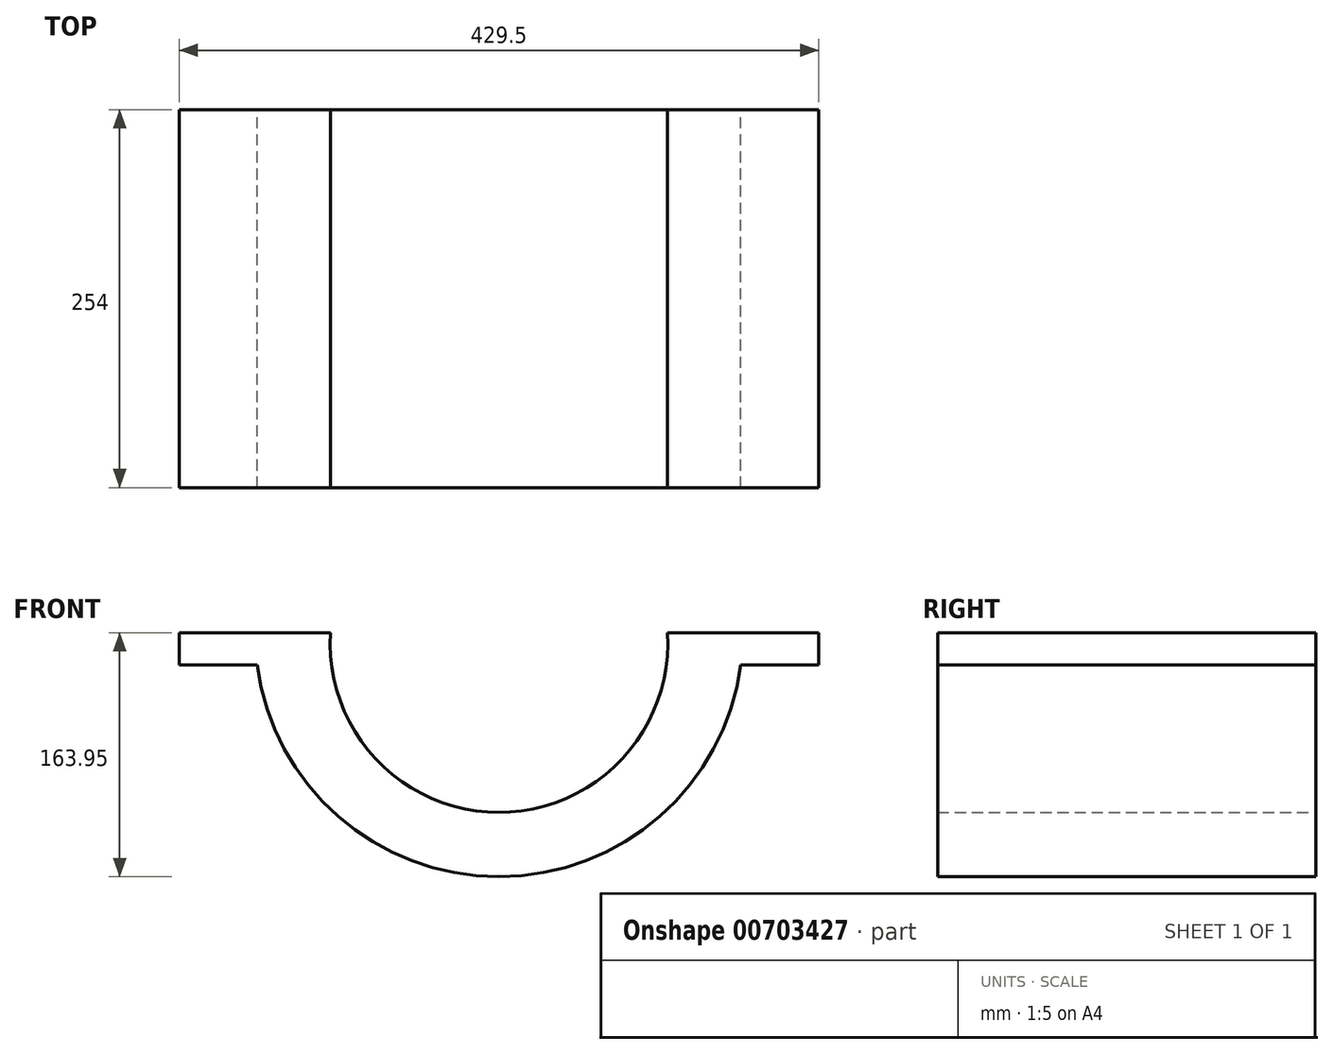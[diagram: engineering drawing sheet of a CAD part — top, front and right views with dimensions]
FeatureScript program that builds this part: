
annotation { "Feature Type Name" : "Feature", "Feature Type Description" : "" }
export const myFeature = defineFeature(function(context is Context, id is Id, definition is map)
    precondition{}
    {
        {
            var Q0;
            Q0=qCreatedBy(makeId("Front.planeOp"),FACE);
            var sketch = newSketch(context, id + "F0", { "sketchPlane" : qUnion([Q0])});
            skLineSegment(sketch, "E0", {"start": v(0, 234.34) * mm, "end": v(0, -237.05) * mm});
            skArc(sketch, "E1", {"start": v(-163.95, 0) * mm, "mid": v(0, -163.95) * mm, "end": v(163.95, 0) * mm});
            skArc(sketch, "E2", {"start": v(163.95, 0) * mm, "mid": v(0, 163.95) * mm, "end": v(-163.95, 0) * mm});
            skLineSegment(sketch, "E3", {"start": v(-113.15, 0) * mm, "end": v(113.15, 0) * mm});
            skLineSegment(sketch, "E4", {"start": v(113.15, 0) * mm, "end": v(113.15, 0) * mm});
            skArc(sketch, "E5", {"start": v(-113.15, 0) * mm, "mid": v(0, -120.64) * mm, "end": v(113.15, 0) * mm});
            skLineSegment(sketch, "E6.bottom", {"start": v(-113.15, 0) * mm, "end": v(-214.75, 0) * mm});
            skLineSegment(sketch, "E6.top", {"start": v(-113.15, -21.53) * mm, "end": v(-214.75, -21.53) * mm});
            skLineSegment(sketch, "E6.left", {"start": v(-113.15, 0) * mm, "end": v(-113.15, -21.53) * mm});
            skLineSegment(sketch, "E6.right", {"start": v(-214.75, 0) * mm, "end": v(-214.75, -21.53) * mm});
            skLineSegment(sketch, "E7.bottom", {"start": v(113.15, 0) * mm, "end": v(214.75, 0) * mm});
            skLineSegment(sketch, "E7.top", {"start": v(113.15, -21.53) * mm, "end": v(214.75, -21.53) * mm});
            skLineSegment(sketch, "E7.left", {"start": v(113.15, 0) * mm, "end": v(113.15, -21.53) * mm});
            skLineSegment(sketch, "E7.right", {"start": v(214.75, 0) * mm, "end": v(214.75, -21.53) * mm});
            skSolve(sketch);
        }
        {
            var Q0;
            {var subQ5=sQuery(id+"F0.wireOp",EDGE,"E6.right");Q0=makeQuery(id+"F0.imprint","IMPRINT",FACE,{"disambiguationData":[TD([[makeQuery(id+"F0.imprint","IMPRINT",EDGE,{"derivedFrom":subQ5}),1.0]])]});}
            var Q1;
            {var subQ5=sQuery(id+"F0.wireOp",EDGE,"E7.right");Q1=makeQuery(id+"F0.imprint","IMPRINT",FACE,{"disambiguationData":[TD([[makeQuery(id+"F0.imprint","IMPRINT",EDGE,{"derivedFrom":subQ5}),-1.0]])]});}
            var Q2;
            {var subQ0=sQuery(id+"F0.wireOp",EDGE,"E1");var subQ1=sQuery(id+"F0.wireOp",EDGE,"E0");var subQ2=makeQuery(id+"F0.imprint","INTERSECT",VERTEX,{"derivedFrom":[subQ1,subQ0]});Q2=makeQuery(id+"F0.imprint","IMPRINT",FACE,{"disambiguationData":[TD([[makeQuery(id+"F0.imprint","IMPRINT",EDGE,{"disambiguationData":[TD([[subQ2,1.0]])],"derivedFrom":subQ1}),-1.0]])]});}
            var Q3;
            {var subQ3=sQuery(id+"F0.wireOp",EDGE,"E1");var subQ6=sQuery(id+"F0.wireOp",EDGE,"E0");var subQ9=makeQuery(id+"F0.imprint","INTERSECT",VERTEX,{"derivedFrom":[subQ6,subQ3]});Q3=makeQuery(id+"F0.imprint","IMPRINT",FACE,{"disambiguationData":[TD([[makeQuery(id+"F0.imprint","IMPRINT",EDGE,{"disambiguationData":[TD([[subQ9,1.0]])],"derivedFrom":subQ6}),1.0]])]});}
            var Q4;
            {var subQ0=sQuery(id+"F0.wireOp",EDGE,"E6.left");var subQ1=sQuery(id+"F0.wireOp",EDGE,"E6.top");var subQ2=makeQuery(id+"F0.imprint","INTERSECT",VERTEX,{"derivedFrom":[subQ1,subQ0]});Q4=makeQuery(id+"F0.imprint","IMPRINT",FACE,{"disambiguationData":[TD([[makeQuery(id+"F0.imprint","IMPRINT",EDGE,{"disambiguationData":[TD([[subQ2,-1.0]])],"derivedFrom":subQ1}),-1.0]])]});}
            var Q5;
            {var subQ3=sQuery(id+"F0.wireOp",EDGE,"E7.left");var subQ6=sQuery(id+"F0.wireOp",EDGE,"E7.top");var subQ7=makeQuery(id+"F0.imprint","INTERSECT",VERTEX,{"derivedFrom":[subQ6,subQ3]});Q5=makeQuery(id+"F0.imprint","IMPRINT",FACE,{"disambiguationData":[TD([[makeQuery(id+"F0.imprint","IMPRINT",EDGE,{"disambiguationData":[TD([[subQ7,-1.0]])],"derivedFrom":subQ6}),1.0]])]});}
            extrude(context, id + "F1", {"entities" : qUnion([Q0, Q1, Q2, Q3, Q4, Q5]), "endBound" : BoundingType.SYMMETRIC, "depth" : 254 * mm, "offsetDistance" : 25.4 * mm});
        }
    });
